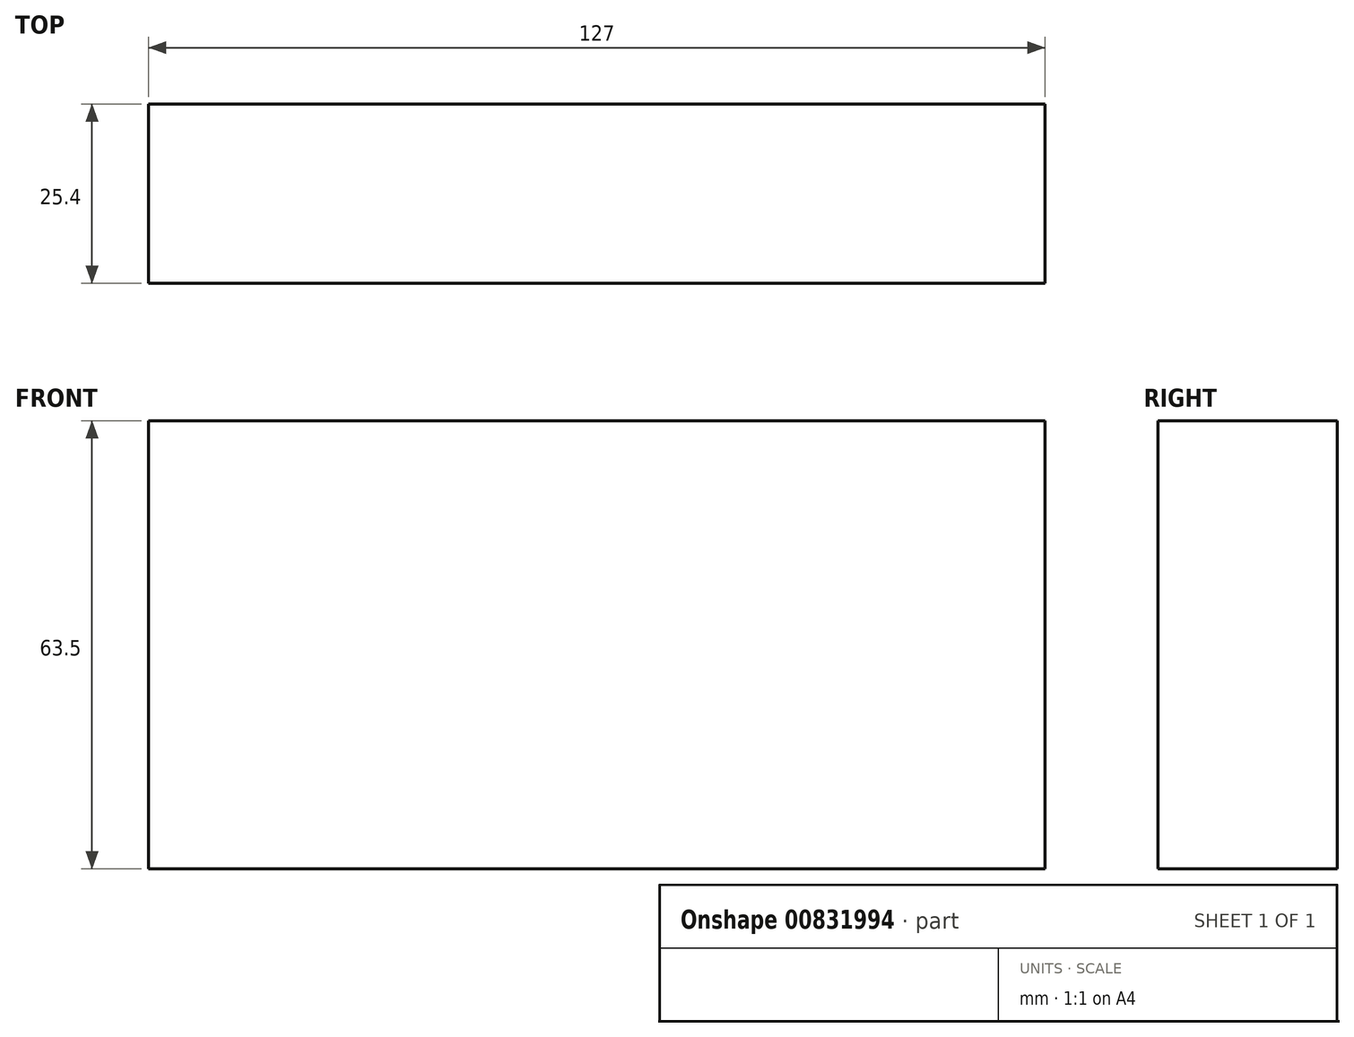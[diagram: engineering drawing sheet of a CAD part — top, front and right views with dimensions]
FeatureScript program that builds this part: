
annotation { "Feature Type Name" : "Feature", "Feature Type Description" : "" }
export const myFeature = defineFeature(function(context is Context, id is Id, definition is map)
    precondition{}
    {
        {
            var Q0;
            Q0=qCreatedBy(makeId("Front.planeOp"),FACE);
            var sketch = newSketch(context, id + "F0", { "sketchPlane" : qUnion([Q0])});
            skLineSegment(sketch, "E0.bottom", {"start": v(63.5, 31.75) * mm, "end": v(-63.5, 31.75) * mm});
            skLineSegment(sketch, "E0.top", {"start": v(63.5, -31.75) * mm, "end": v(-63.5, -31.75) * mm});
            skLineSegment(sketch, "E0.left", {"start": v(63.5, 31.75) * mm, "end": v(63.5, -31.75) * mm});
            skLineSegment(sketch, "E0.right", {"start": v(-63.5, 31.75) * mm, "end": v(-63.5, -31.75) * mm});
            skPoint(sketch, "E0.middle", {"position": v(0, 0) * mm});
            skSolve(sketch);
        }
        {
            var Q0;
            Q0=makeQuery(id+"F0.imprint","IMPRINT",FACE,{"disambiguationData":[TD([[makeQuery(id+"F0.imprint","IMPRINT",EDGE,{"derivedFrom":sQuery(id+"F0.wireOp",EDGE,"E0.bottom")}),1.0]])]});
            extrude(context, id + "F1", {"entities" : qUnion([Q0]), "oppositeDirection" : true, "depth" : 25.4 * mm, "offsetDistance" : 25.4 * mm});
        }
    });
